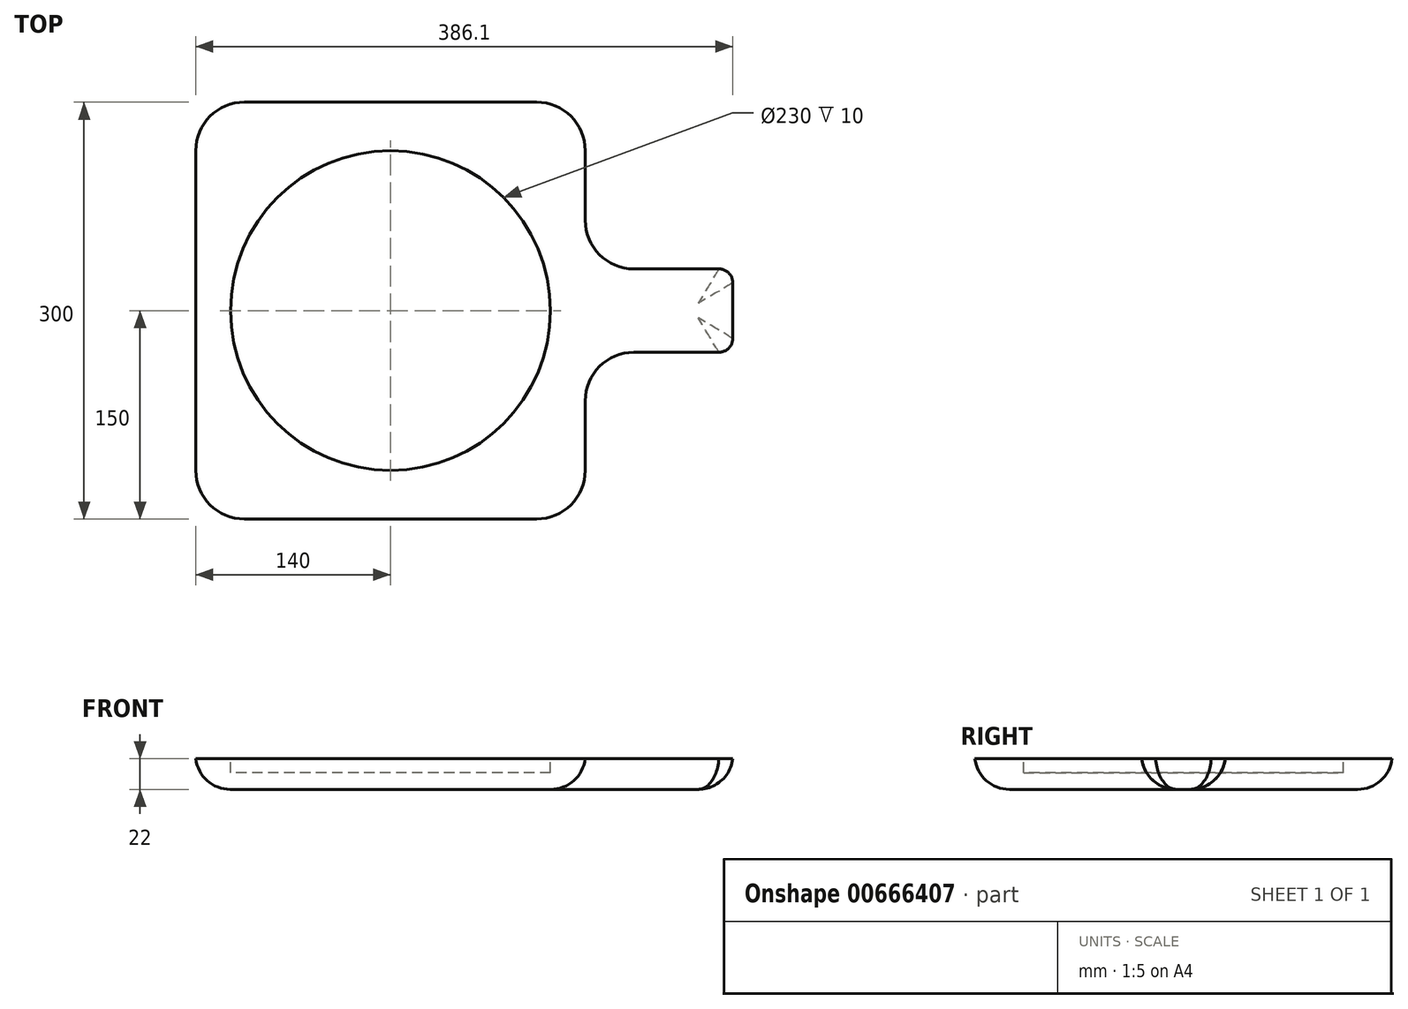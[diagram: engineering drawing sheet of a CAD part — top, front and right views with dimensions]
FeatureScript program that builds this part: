
annotation { "Feature Type Name" : "Feature", "Feature Type Description" : "" }
export const myFeature = defineFeature(function(context is Context, id is Id, definition is map)
    precondition{}
    {
        {
            var Q0;
            Q0=qCreatedBy(makeId("Top.planeOp"),FACE);
            var sketch = newSketch(context, id + "F0", { "sketchPlane" : qUnion([Q0])});
            skCircle(sketch, "E0", {"center": v(0, 0) * mm, "radius": 55 * mm});
            skCircle(sketch, "E1.0", {"center": v(0, 0) * mm, "radius": 115 * mm});
            skPoint(sketch, "E2.start.orphan", {"position": v(34.31, 0) * mm});
            skLineSegment(sketch, "E3", {"start": v(-140, 0) * mm, "end": v(0, 0) * mm});
            skLineSegment(sketch, "E4.0", {"start": v(-140, -150) * mm, "end": v(140, -150) * mm});
            skLineSegment(sketch, "E5.0", {"start": v(-140, 150) * mm, "end": v(140, 150) * mm});
            skLineSegment(sketch, "E6", {"start": v(-140, 150) * mm, "end": v(-140, -150) * mm});
            skLineSegment(sketch, "E7.trimOffspring", {"start": v(34.31, 0) * mm, "end": v(246.1, 0) * mm});
            skLineSegment(sketch, "E8", {"start": v(140, 150) * mm, "end": v(140, -150) * mm});
            skLineSegment(sketch, "E9.0", {"start": v(46.1, -30) * mm, "end": v(246.1, -30) * mm});
            skLineSegment(sketch, "E10.0", {"start": v(46.1, 30) * mm, "end": v(246.1, 30) * mm});
            skLineSegment(sketch, "E11", {"start": v(246.1, 30) * mm, "end": v(246.1, -30) * mm});
            skPoint(sketch, "E12.orphan", {"position": v(-216.03, 0) * mm});
            skSolve(sketch);
        }
        {
            var Q0;
            Q0=qCreatedBy(makeId("Top.planeOp"),FACE);
            var sketch = newSketch(context, id + "F1", { "sketchPlane" : qUnion([Q0])});
            skLineSegment(sketch, "E13.0", {"start": v(-140, 150) * mm, "end": v(-140, -150) * mm});
            skLineSegment(sketch, "E13.1", {"start": v(-140, 150) * mm, "end": v(140, 150) * mm});
            skLineSegment(sketch, "E13.2", {"start": v(140, 150) * mm, "end": v(140, 30) * mm});
            skLineSegment(sketch, "E13.3", {"start": v(140, 30) * mm, "end": v(246.1, 30) * mm});
            skLineSegment(sketch, "E13.4", {"start": v(140, -30) * mm, "end": v(246.1, -30) * mm});
            skLineSegment(sketch, "E13.5", {"start": v(246.1, 30) * mm, "end": v(246.1, -30) * mm});
            skLineSegment(sketch, "E13.6", {"start": v(-140, -150) * mm, "end": v(140, -150) * mm});
            skPoint(sketch, "E14.orphan", {"position": v(46.1, 30) * mm});
            skPoint(sketch, "E15.orphan", {"position": v(46.1, -30) * mm});
            skLineSegment(sketch, "E16.trimOffspring", {"start": v(140, -30) * mm, "end": v(140, -150) * mm});
            skSolve(sketch);
        }
        {
            var Q0;
            Q0 = qSketchRegion(id + "F1", true);
            extrude(context, id + "F2", {"entities" : qUnion([Q0]), "depth" : 22 * mm, "offsetDistance" : 25 * mm});
        }
        {
            var Q0;
            Q0=makeQuery(id+"F2.opExtrude","SWEPT_EDGE",EDGE,{"disambiguationData":[OSD([sQuery(id+"F1.wireOp",EDGE,"E13.0"),sQuery(id+"F1.wireOp",EDGE,"E13.6")])]});
            var Q1;
            Q1=makeQuery(id+"F2.opExtrude","SWEPT_EDGE",EDGE,{"disambiguationData":[OSD([sQuery(id+"F1.wireOp",EDGE,"E13.6"),sQuery(id+"F1.wireOp",EDGE,"E16.trimOffspring")])]});
            var Q2;
            Q2=makeQuery(id+"F2.opExtrude","SWEPT_EDGE",EDGE,{"disambiguationData":[OSD([sQuery(id+"F1.wireOp",EDGE,"E13.4"),sQuery(id+"F1.wireOp",EDGE,"E16.trimOffspring")])]});
            var Q3;
            Q3=makeQuery(id+"F2.opExtrude","SWEPT_EDGE",EDGE,{"disambiguationData":[OSD([sQuery(id+"F1.wireOp",EDGE,"E13.1"),sQuery(id+"F1.wireOp",EDGE,"E13.2")])]});
            var Q4;
            Q4=makeQuery(id+"F2.opExtrude","SWEPT_EDGE",EDGE,{"disambiguationData":[OSD([sQuery(id+"F1.wireOp",EDGE,"E13.2"),sQuery(id+"F1.wireOp",EDGE,"E13.3")])]});
            var Q5;
            Q5=makeQuery(id+"F2.opExtrude","SWEPT_EDGE",EDGE,{"disambiguationData":[OSD([sQuery(id+"F1.wireOp",EDGE,"E13.0"),sQuery(id+"F1.wireOp",EDGE,"E13.1")])]});
            fillet(context, id + "F3", {"entities" : qUnion([Q0, Q1, Q2, Q3, Q4, Q5]), "radius" : 35 * mm, "tangentPropagation" : true, "allowEdgeOverflow" : false});
        }
        {
            var Q0;
            Q0=makeQuery(id+"F2.opExtrude","CAP_FACE",FACE,{"disambiguationData":[OSD([sQuery(id+"F1.wireOp",EDGE,"E13.0"),sQuery(id+"F1.wireOp",EDGE,"E13.1"),sQuery(id+"F1.wireOp",EDGE,"E13.2"),sQuery(id+"F1.wireOp",EDGE,"E13.3"),sQuery(id+"F1.wireOp",EDGE,"E13.4"),sQuery(id+"F1.wireOp",EDGE,"E13.5"),sQuery(id+"F1.wireOp",EDGE,"E13.6"),sQuery(id+"F1.wireOp",EDGE,"E16.trimOffspring")])],"isStart":false});
            var sketch = newSketch(context, id + "F4", { "sketchPlane" : qUnion([Q0])});
            skCircle(sketch, "E17.0", {"center": v(0, 0) * mm, "radius": 115 * mm});
            skSolve(sketch);
        }
        {
            var Q0;
            Q0 = qSketchRegion(id + "F4", true);
            extrude(context, id + "F5", {"entities" : qUnion([Q0]), "operationType" : NewBodyOperationType.REMOVE, "oppositeDirection" : true, "depth" : 10 * mm, "offsetDistance" : 25 * mm});
        }
        {
            var Q0;
            Q0=makeQuery(id+"F2.opExtrude","SWEPT_EDGE",EDGE,{"disambiguationData":[OSD([sQuery(id+"F1.wireOp",EDGE,"E13.4"),sQuery(id+"F1.wireOp",EDGE,"E13.5")])]});
            var Q1;
            Q1=makeQuery(id+"F2.opExtrude","SWEPT_EDGE",EDGE,{"disambiguationData":[OSD([sQuery(id+"F1.wireOp",EDGE,"E13.3"),sQuery(id+"F1.wireOp",EDGE,"E13.5")])]});
            fillet(context, id + "F6", {"entities" : qUnion([Q0, Q1]), "radius" : 10 * mm, "tangentPropagation" : true, "allowEdgeOverflow" : false});
        }
        {
            var Q0;
            Q0=makeQuery(id+"F2.opExtrude","CAP_FACE",FACE,{"disambiguationData":[OSD([sQuery(id+"F1.wireOp",EDGE,"E13.0"),sQuery(id+"F1.wireOp",EDGE,"E13.1"),sQuery(id+"F1.wireOp",EDGE,"E13.2"),sQuery(id+"F1.wireOp",EDGE,"E13.3"),sQuery(id+"F1.wireOp",EDGE,"E13.4"),sQuery(id+"F1.wireOp",EDGE,"E13.5"),sQuery(id+"F1.wireOp",EDGE,"E13.6"),sQuery(id+"F1.wireOp",EDGE,"E16.trimOffspring")])],"isStart":true});
            fillet(context, id + "F7", {"entities" : qUnion([Q0]), "radius" : 25 * mm, "tangentPropagation" : true, "allowEdgeOverflow" : false});
        }
    });
